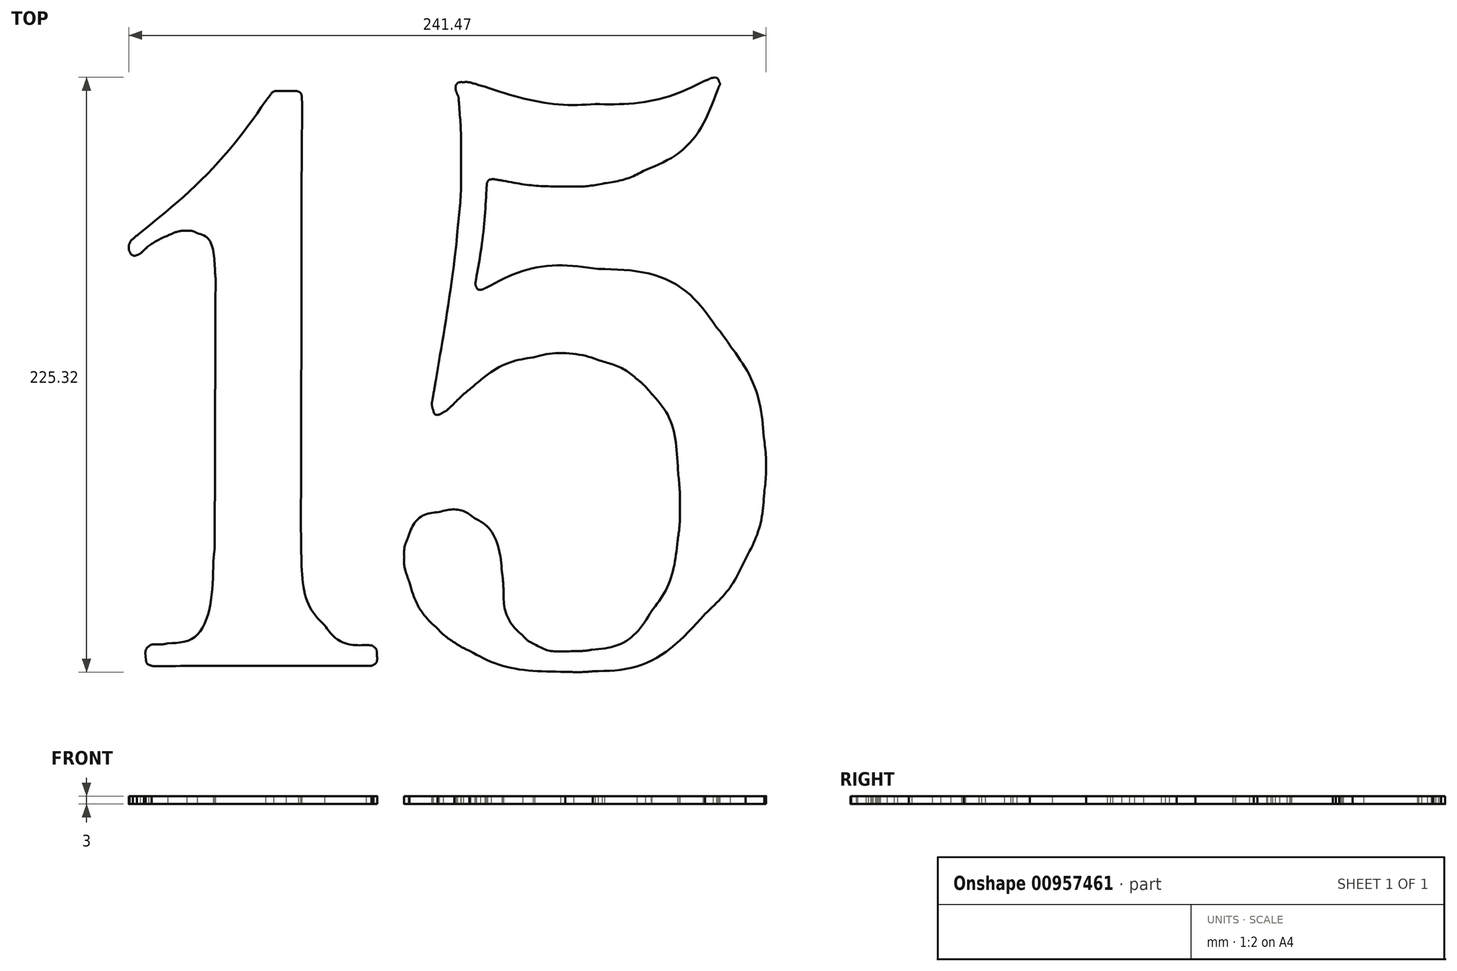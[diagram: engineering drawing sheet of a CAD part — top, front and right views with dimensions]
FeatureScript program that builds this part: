
annotation { "Feature Type Name" : "Feature", "Feature Type Description" : "" }
export const myFeature = defineFeature(function(context is Context, id is Id, definition is map)
    precondition{}
    {
        {
            var Q0;
            Q0=qCreatedBy(makeId("Top.planeOp"),FACE);
            var sketch = newSketch(context, id + "F0", { "sketchPlane" : qUnion([Q0])});
            skLineSegment(sketch, "E0", {"start": v(-24.42, -105.17) * mm, "end": v(-24.97, -105.5) * mm});
            skLineSegment(sketch, "E1", {"start": v(-24.97, -105.5) * mm, "end": v(-66.43, -105.53) * mm});
            skFitSpline(sketch, "E2", {"points": [v(48.48, -107.7) * mm, v(34.05, -107.18) * mm, v(22.01, -104.56) * mm, v(12.15, -99.8) * mm]});
            skFitSpline(sketch, "E3", {"points": [v(12.15, -99.8) * mm, v(9.58, -98.57) * mm, v(8.4, -97.9) * mm, v(6.4, -96.59) * mm]});
            skFitSpline(sketch, "E4", {"points": [v(6.4, -96.59) * mm, v(4.1, -95.06) * mm, v(2.12, -93.45) * mm, v(0.07, -91.4) * mm]});
            skFitSpline(sketch, "E5", {"points": [v(0.07, -91.4) * mm, v(-4.76, -86.56) * mm, v(-8.22, -80.85) * mm, v(-10.66, -73.69) * mm]});
            skFitSpline(sketch, "E6", {"points": [v(-10.66, -73.69) * mm, v(-12.13, -69.35) * mm, v(-12.56, -67.2) * mm, v(-12.56, -64.23) * mm]});
            skFitSpline(sketch, "E7", {"points": [v(-12.56, -64.23) * mm, v(-12.56, -61.4) * mm, v(-12.12, -59.24) * mm, v(-11.05, -56.79) * mm]});
            skFitSpline(sketch, "E8", {"points": [v(-11.05, -56.79) * mm, v(-8.74, -51.44) * mm, v(-4.83, -48.26) * mm, v(0.74, -47.19) * mm]});
            skFitSpline(sketch, "E9", {"points": [v(0.74, -47.19) * mm, v(5.72, -46.22) * mm, v(10.38, -47.04) * mm, v(14.1, -49.53) * mm]});
            skFitSpline(sketch, "E10", {"points": [v(14.1, -49.53) * mm, v(19.28, -53) * mm, v(23.15, -60.58) * mm, v(24.47, -69.88) * mm]});
            skFitSpline(sketch, "E11", {"points": [v(24.47, -69.88) * mm, v(24.75, -71.85) * mm, v(24.88, -73.34) * mm, v(25.1, -76.9) * mm]});
            skFitSpline(sketch, "E12", {"points": [v(25.1, -76.9) * mm, v(25.5, -83.56) * mm, v(28.04, -89.56) * mm, v(32.31, -93.97) * mm]});
            skFitSpline(sketch, "E13", {"points": [v(32.31, -93.97) * mm, v(33.79, -95.5) * mm, v(35.01, -96.38) * mm, v(36.9, -97.31) * mm]});
            skFitSpline(sketch, "E14", {"points": [v(36.9, -97.31) * mm, v(40.96, -99.32) * mm, v(44.94, -100.01) * mm, v(51.62, -99.88) * mm]});
            skFitSpline(sketch, "E15", {"points": [v(51.62, -99.88) * mm, v(55.1, -99.82) * mm, v(56.31, -99.72) * mm, v(58.58, -99.34) * mm]});
            skFitSpline(sketch, "E16", {"points": [v(58.58, -99.34) * mm, v(67.85, -97.8) * mm, v(75.39, -92.9) * mm, v(81.17, -84.67) * mm]});
            skFitSpline(sketch, "E17", {"points": [v(81.17, -84.67) * mm, v(86.07, -77.68) * mm, v(89.56, -68.3) * mm, v(90.99, -58.24) * mm]});
            skFitSpline(sketch, "E18", {"points": [v(90.99, -58.24) * mm, v(91.63, -53.67) * mm, v(91.85, -50.32) * mm, v(91.85, -44.86) * mm]});
            skFitSpline(sketch, "E19", {"points": [v(91.85, -44.86) * mm, v(91.85, -39.85) * mm, v(91.75, -37.96) * mm, v(91.16, -31.42) * mm]});
            skFitSpline(sketch, "E20", {"points": [v(91.16, -31.42) * mm, v(90, -18.76) * mm, v(86.78, -9.53) * mm, v(80.96, -2.17) * mm]});
            skFitSpline(sketch, "E21", {"points": [v(80.96, -2.17) * mm, v(79.82, -0.74) * mm, v(77.1, 1.97) * mm, v(75.64, 3.14) * mm]});
            skFitSpline(sketch, "E22", {"points": [v(75.64, 3.14) * mm, v(71.98, 6.06) * mm, v(67.43, 8.39) * mm, v(62.41, 9.92) * mm]});
            skFitSpline(sketch, "E23", {"points": [v(62.41, 9.92) * mm, v(54.57, 12.3) * mm, v(43.8, 12.91) * mm, v(36.25, 11.38) * mm]});
            skFitSpline(sketch, "E24", {"points": [v(36.25, 11.38) * mm, v(28.25, 9.76) * mm, v(20.33, 5.82) * mm, v(12.71, -0.32) * mm]});
            skFitSpline(sketch, "E25", {"points": [v(12.71, -0.32) * mm, v(10.53, -2.08) * mm, v(8.66, -3.75) * mm, v(6.23, -6.13) * mm]});
            skFitSpline(sketch, "E26", {"points": [v(6.23, -6.13) * mm, v(3.94, -8.37) * mm, v(3.5, -8.74) * mm, v(2.21, -9.4) * mm]});
            skFitSpline(sketch, "E27", {"points": [v(2.21, -9.4) * mm, v(0.29, -10.38) * mm, v(-1.01, -10.07) * mm, v(-1.59, -8.5) * mm]});
            skFitSpline(sketch, "E28", {"points": [v(-1.59, -8.5) * mm, v(-1.91, -7.6) * mm, v(-2.07, -6) * mm, v(-1.93, -5.09) * mm]});
            skFitSpline(sketch, "E29", {"points": [v(-1.93, -5.09) * mm, v(-1.86, -4.66) * mm, v(-1.26, -1.14) * mm, v(-0.6, 2.74) * mm]});
            skFitSpline(sketch, "E30", {"points": [v(-0.6, 2.74) * mm, v(2.75, 22.66) * mm, v(6.46, 48.16) * mm, v(7.59, 59.1) * mm]});
            skFitSpline(sketch, "E31", {"points": [v(7.59, 59.1) * mm, v(8.57, 68.72) * mm, v(8.97, 76.67) * mm, v(8.97, 86.6) * mm]});
            skFitSpline(sketch, "E32", {"points": [v(8.97, 86.6) * mm, v(8.97, 94.45) * mm, v(8.78, 99.58) * mm, v(8.2, 107.27) * mm]});
            skFitSpline(sketch, "E33", {"points": [v(8.2, 107.27) * mm, v(8, 110.07) * mm, v(7.96, 110.26) * mm, v(7.41, 111.5) * mm]});
            skFitSpline(sketch, "E34", {"points": [v(7.41, 111.5) * mm, v(7.1, 112.18) * mm, v(6.98, 112.66) * mm, v(6.94, 113.2) * mm]});
            skFitSpline(sketch, "E35", {"points": [v(6.94, 113.2) * mm, v(6.87, 114.16) * mm, v(6.94, 114.45) * mm, v(7.38, 114.95) * mm]});
            skFitSpline(sketch, "E36", {"points": [v(7.38, 114.95) * mm, v(7.84, 115.47) * mm, v(8.57, 115.68) * mm, v(9.91, 115.68) * mm]});
            skFitSpline(sketch, "E37", {"points": [v(9.91, 115.68) * mm, v(11.67, 115.68) * mm, v(13.12, 115.37) * mm, v(17.92, 113.93) * mm]});
            skFitSpline(sketch, "E38", {"points": [v(17.92, 113.93) * mm, v(33.08, 109.4) * mm, v(47.52, 107.13) * mm, v(59.77, 107.36) * mm]});
            skFitSpline(sketch, "E39", {"points": [v(59.77, 107.36) * mm, v(73.93, 107.63) * mm, v(89.09, 110.78) * mm, v(100.65, 115.86) * mm]});
            skFitSpline(sketch, "E40", {"points": [v(100.65, 115.86) * mm, v(103.7, 117.2) * mm, v(103.95, 117.3) * mm, v(104.45, 117.35) * mm]});
            skFitSpline(sketch, "E41", {"points": [v(104.45, 117.35) * mm, v(105.42, 117.46) * mm, v(106.32, 116.9) * mm, v(106.75, 115.89) * mm]});
            skFitSpline(sketch, "E42", {"points": [v(106.75, 115.89) * mm, v(107.1, 115.1) * mm, v(107.02, 114.72) * mm, v(106.18, 112.8) * mm]});
            skFitSpline(sketch, "E43", {"points": [v(106.18, 112.8) * mm, v(99.95, 98.53) * mm, v(90.85, 88.41) * mm, v(78.85, 82.42) * mm]});
            skFitSpline(sketch, "E44", {"points": [v(78.85, 82.42) * mm, v(73.9, 79.94) * mm, v(69, 78.35) * mm, v(63.27, 77.35) * mm]});
            skFitSpline(sketch, "E45", {"points": [v(63.27, 77.35) * mm, v(57.8, 76.4) * mm, v(53.37, 76.1) * mm, v(46.67, 76.19) * mm]});
            skFitSpline(sketch, "E46", {"points": [v(46.67, 76.19) * mm, v(39.53, 76.29) * mm, v(32.99, 76.93) * mm, v(24.98, 78.31) * mm]});
            skFitSpline(sketch, "E47", {"points": [v(24.98, 78.31) * mm, v(21.07, 78.99) * mm, v(21.04, 78.99) * mm, v(20.39, 78.86) * mm]});
            skFitSpline(sketch, "E48", {"points": [v(20.39, 78.86) * mm, v(19.68, 78.71) * mm, v(19.3, 78.43) * mm, v(18.98, 77.82) * mm]});
            skFitSpline(sketch, "E49", {"points": [v(18.98, 77.82) * mm, v(18.79, 77.44) * mm, v(18.72, 76.96) * mm, v(18.6, 74.87) * mm]});
            skFitSpline(sketch, "E50", {"points": [v(18.6, 74.87) * mm, v(17.9, 64.06) * mm, v(16.54, 52.1) * mm, v(14.86, 42.1) * mm]});
            skFitSpline(sketch, "E51", {"points": [v(14.86, 42.1) * mm, v(14.43, 39.54) * mm, v(14.42, 38.9) * mm, v(14.81, 38.02) * mm]});
            skFitSpline(sketch, "E52", {"points": [v(14.81, 38.02) * mm, v(15.1, 37.38) * mm, v(15.6, 37.08) * mm, v(16.38, 37.08) * mm]});
            skFitSpline(sketch, "E53", {"points": [v(16.38, 37.08) * mm, v(16.88, 37.08) * mm, v(17.23, 37.2) * mm, v(18.53, 37.8) * mm]});
            skFitSpline(sketch, "E54", {"points": [v(18.53, 37.8) * mm, v(31.59, 43.9) * mm, v(45.77, 46.28) * mm, v(60.95, 44.92) * mm]});
            skFitSpline(sketch, "E55", {"points": [v(60.95, 44.92) * mm, v(79.96, 43.21) * mm, v(94.9, 35.85) * mm, v(105.75, 22.82) * mm]});
            skFitSpline(sketch, "E56", {"points": [v(105.75, 22.82) * mm, v(107.36, 20.89) * mm, v(109.42, 18.1) * mm, v(110.99, 15.73) * mm]});
            skFitSpline(sketch, "E57", {"points": [v(110.99, 15.73) * mm, v(117.9, 5.3) * mm, v(122.14, -6.21) * mm, v(123.63, -18.6) * mm]});
            skFitSpline(sketch, "E58", {"points": [v(123.63, -18.6) * mm, v(124.36, -24.65) * mm, v(124.46, -33.8) * mm, v(123.85, -39.9) * mm]});
            skFitSpline(sketch, "E59", {"points": [v(123.85, -39.9) * mm, v(122.97, -48.86) * mm, v(120.63, -57.08) * mm, v(116.73, -64.9) * mm]});
            skFitSpline(sketch, "E60", {"points": [v(116.73, -64.9) * mm, v(112.85, -72.7) * mm, v(108.16, -79.12) * mm, v(101.45, -85.8) * mm]});
            skFitSpline(sketch, "E61", {"points": [v(101.45, -85.8) * mm, v(88.22, -98.97) * mm, v(74.33, -106.06) * mm, v(58.84, -107.54) * mm]});
            skFitSpline(sketch, "E62", {"points": [v(58.84, -107.54) * mm, v(56.57, -107.75) * mm, v(51.86, -107.83) * mm, v(48.48, -107.7) * mm]});
            skFitSpline(sketch, "E63", {"points": [v(-108.3, -105.4) * mm, v(-109.67, -104.92) * mm, v(-110.33, -103.91) * mm, v(-110.5, -102.04) * mm]});
            skFitSpline(sketch, "E64", {"points": [v(-110.5, -102.04) * mm, v(-110.64, -100.41) * mm, v(-110.19, -98.87) * mm, v(-109.35, -98.13) * mm]});
            skFitSpline(sketch, "E65", {"points": [v(-109.35, -98.13) * mm, v(-108.69, -97.54) * mm, v(-108.15, -97.4) * mm, v(-106.37, -97.37) * mm]});
            skFitSpline(sketch, "E66", {"points": [v(-106.37, -97.37) * mm, v(-104.32, -97.32) * mm, v(-103.46, -97.24) * mm, v(-102.2, -96.96) * mm]});
            skFitSpline(sketch, "E67", {"points": [v(-102.2, -96.96) * mm, v(-92.28, -94.83) * mm, v(-86.49, -84.43) * mm, v(-84.86, -65.81) * mm]});
            skFitSpline(sketch, "E68", {"points": [v(-84.86, -65.81) * mm, v(-84.37, -60.18) * mm, v(-84.37, -60.15) * mm, v(-84.23, -15.04) * mm]});
            skFitSpline(sketch, "E69", {"points": [v(-84.23, -15.04) * mm, v(-84.07, 35.43) * mm, v(-84.07, 41.37) * mm, v(-84.22, 43.23) * mm]});
            skFitSpline(sketch, "E70", {"points": [v(-84.22, 43.23) * mm, v(-84.91, 51.64) * mm, v(-87.12, 56.64) * mm, v(-90.94, 58.48) * mm]});
            skFitSpline(sketch, "E71", {"points": [v(-90.94, 58.48) * mm, v(-92.27, 59.11) * mm, v(-93.26, 59.33) * mm, v(-94.9, 59.33) * mm]});
            skFitSpline(sketch, "E72", {"points": [v(-94.9, 59.33) * mm, v(-97.05, 59.33) * mm, v(-99.39, 58.75) * mm, v(-102.2, 57.52) * mm]});
            skFitSpline(sketch, "E73", {"points": [v(-102.2, 57.52) * mm, v(-105.02, 56.28) * mm, v(-109.38, 53.6) * mm, v(-111.15, 52) * mm]});
            skFitSpline(sketch, "E74", {"points": [v(-111.15, 52) * mm, v(-112.24, 51.02) * mm, v(-113.13, 50.41) * mm, v(-113.88, 50.16) * mm]});
            skFitSpline(sketch, "E75", {"points": [v(-113.88, 50.16) * mm, v(-114.56, 49.92) * mm, v(-114.96, 49.9) * mm, v(-115.43, 50.1) * mm]});
            skFitSpline(sketch, "E76", {"points": [v(-115.43, 50.1) * mm, v(-115.93, 50.32) * mm, v(-116.23, 50.67) * mm, v(-116.6, 51.48) * mm]});
            skFitSpline(sketch, "E77", {"points": [v(-116.6, 51.48) * mm, v(-116.87, 52.04) * mm, v(-116.92, 52.3) * mm, v(-116.92, 53.06) * mm]});
            skFitSpline(sketch, "E78", {"points": [v(-116.92, 53.06) * mm, v(-116.92, 53.85) * mm, v(-116.88, 54.06) * mm, v(-116.56, 54.7) * mm]});
            skFitSpline(sketch, "E79", {"points": [v(-116.56, 54.7) * mm, v(-116.13, 55.58) * mm, v(-115.55, 56.16) * mm, v(-112.58, 58.65) * mm]});
            skFitSpline(sketch, "E80", {"points": [v(-112.58, 58.65) * mm, v(-94.5, 73.84) * mm, v(-77.66, 91.5) * mm, v(-65.06, 108.51) * mm]});
            skFitSpline(sketch, "E81", {"points": [v(-65.06, 108.51) * mm, v(-62.67, 111.74) * mm, v(-62.6, 111.83) * mm, v(-62.05, 112.08) * mm]});
            skFitSpline(sketch, "E82", {"points": [v(-62.05, 112.08) * mm, v(-61.62, 112.27) * mm, v(-61.24, 112.29) * mm, v(-57.35, 112.29) * mm]});
            skFitSpline(sketch, "E83", {"points": [v(-57.35, 112.29) * mm, v(-53.48, 112.29) * mm, v(-53.07, 112.27) * mm, v(-52.66, 112.08) * mm]});
            skFitSpline(sketch, "E84", {"points": [v(-52.66, 112.08) * mm, v(-52.1, 111.83) * mm, v(-51.63, 111.3) * mm, v(-51.48, 110.72) * mm]});
            skFitSpline(sketch, "E85", {"points": [v(-51.48, 110.72) * mm, v(-51.4, 110.41) * mm, v(-51.41, 84.93) * mm, v(-51.53, 26.84) * mm]});
            skFitSpline(sketch, "E86", {"points": [v(-51.53, 26.84) * mm, v(-51.63, -26.14) * mm, v(-51.65, -57.53) * mm, v(-51.59, -59.15) * mm]});
            skFitSpline(sketch, "E87", {"points": [v(-51.59, -59.15) * mm, v(-50.98, -73.69) * mm, v(-48.14, -83.6) * mm, v(-42.72, -90.1) * mm]});
            skFitSpline(sketch, "E88", {"points": [v(-42.72, -90.1) * mm, v(-38.89, -94.68) * mm, v(-33.38, -97.31) * mm, v(-26.97, -97.61) * mm]});
            skFitSpline(sketch, "E89", {"points": [v(-26.97, -97.61) * mm, v(-25.23, -97.7) * mm, v(-24.5, -97.88) * mm, v(-23.93, -98.4) * mm]});
            skFitSpline(sketch, "E90", {"points": [v(-23.93, -98.4) * mm, v(-23.26, -99) * mm, v(-22.99, -99.75) * mm, v(-22.93, -101.16) * mm]});
            skFitSpline(sketch, "E91", {"points": [v(-22.93, -101.16) * mm, v(-22.84, -103.17) * mm, v(-23.34, -104.5) * mm, v(-24.42, -105.17) * mm]});
            skFitSpline(sketch, "E92", {"points": [v(-66.43, -105.53) * mm, v(-100.14, -105.55) * mm, v(-107.97, -105.53) * mm, v(-108.3, -105.4) * mm]});
            skLineSegment(sketch, "E93.bottom", {"start": v(-134.4, 133) * mm, "end": v(146.6, 133) * mm, "construction": true});
            skLineSegment(sketch, "E93.top", {"start": v(-134.4, -117) * mm, "end": v(146.6, -117) * mm, "construction": true});
            skLineSegment(sketch, "E93.left", {"start": v(-134.4, 133) * mm, "end": v(-134.4, -117) * mm, "construction": true});
            skLineSegment(sketch, "E93.right", {"start": v(146.6, 133) * mm, "end": v(146.6, -117) * mm, "construction": true});
            skSolve(sketch);
        }
        {
            var Q0;
            Q0=makeQuery(id+"F0.imprint","IMPRINT",FACE,{"disambiguationData":[TD([[makeQuery(id+"F0.imprint","IMPRINT",EDGE,{"derivedFrom":sQuery(id+"F0.wireOp",EDGE,"E0")}),-1.0]])]});
            var Q1;
            Q1=makeQuery(id+"F0.imprint","IMPRINT",FACE,{"disambiguationData":[TD([[makeQuery(id+"F0.imprint","IMPRINT",EDGE,{"derivedFrom":sQuery(id+"F0.wireOp",EDGE,"E2")}),-1.0]])]});
            extrude(context, id + "F1", {"entities" : qUnion([Q0, Q1]), "depth" : 3 * mm, "offsetDistance" : 25 * mm});
        }
    });
